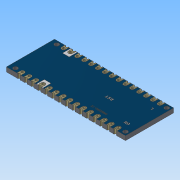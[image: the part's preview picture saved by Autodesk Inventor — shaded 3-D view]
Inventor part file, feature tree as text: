
AUTODESK INVENTOR PART (.ipt)
format: ipt  version: 2016 (Build 200138000, 138)  size: 3,481,600 bytes
history: native  units: mm
features: extrude x6, projected_geometry x6, sketch x5, other x3, hole x2, mirror x2, pattern_linear x1
ambient origin geometry x8: Origin, YZ Plane, XZ Plane, XY Plane, X Axis, Y Axis, Z Axis, Center Point
bodies: Body1 (feature_tree)
feature tree (25):
  other  "Blocks"
  extrude  "Extrusion4"  Depth=17.78mm
  sketch  "Sketch11"  dims[d9=1.6mm d10=0.0mm d11=1.27mm]
  hole  "Hole1"  [1 undecoded]
  hole  "Hole2"  [1 undecoded]
  extrude  "Extrusion5"  Depth=3.81mm
  pattern_linear  "Rectangular Pattern1"  Count1=15 Spacing1=35.56mm
  mirror  "Mirror1"
  mirror  "Mirror2"
  extrude  "Extrusion7"  Depth=1.6mm
  sketch  "Sketch15"  dims[d16=1.6mm d17=6.0mm d18=4.0mm d19=2.0mm d20=90.0deg d21=8.0mm d22=20.594885mm d23=0.9mm d24=6.0mm d25=4.0mm d26=2.0mm d27=90.0deg d28=8.0mm d29=20.594885mm d30=150.0mm d32=35.56mm d33=1.1mm d34=1.5mm d36=0.05mm d37=0.0mm d39=35.56mm d40=2.54mm d41=44.0mm d107=2.5mm d108=3.0mm d110=16.0mm d111=5.7mm d112=0.65mm d113=3.0mm d114=1.0mm d115=1.7mm d116=3.8mm d117=2.9mm d122=2.5mm d123=13.8mm d124=8.2mm d127=0.01mm d128=0.0mm d129=1.75mm d130=1.67mm d131=1.19mm d132=1.11mm d136=3.5mm d137=0.56mm d138=7.0mm d139=7.0mm d140=1.1mm d141=0.45mm d145=9.2mm d146=5.08mm d147=2.54mm d148=2.2mm d151=1.78mm d152=3.43mm d153=0.8mm d154=0.9mm d155=1.0625mm d156=2.7375mm d158=8.005mm d159=1.1mm d160=1.0625mm d161=2.7375mm d163=9.2mm d164=4.9mm d165=1.5mm d166=0.2mm d168=0.2mm d169=5.7mm d170=0.65mm d171=6.7mm d172=12.0mm d173=1.1mm d174=0.48125mm d175=0.103125mm d176=0.103125mm d177=0.103125mm d179=1.1mm d180=0.33mm d181=0.106562mm d182=0.103125mm d183=13.439035mm d184=9.250245mm d185=10.12291mm d186=0.488125mm d187=0.910937mm d193=1.1mm d195=0.055mm d196=0.055mm d197=0.11mm d198=0.935mm d199=0.165mm d200=0.165mm d202=2.55mm d203=0.3mm d204=11.0mm d205=1.0mm d206=0.5mm d209=2.2mm d212=2.2mm d213=90.0deg d214=1.0mm d215=0.9mm d216=0.1mm d218=3.3mm d219=0.1mm d221=8.0125mm d222=3.475mm d228=0.2mm d229=2.6mm d230=3.7mm d231=0.3mm d232=0.3mm d233=0.3mm d234=0.01mm d235=0.0mm d236=0.01mm d237=0.0mm d238=0.1mm d239=0.0mm d240=0.1mm d241=100.0mm d243=0.355556mm d244=10.0mm d246=10.0mm d250=80.0mm d252=0.3mm d253=10.0mm d255=10.0mm d257=0.05mm d258=0.05mm d259=3.7mm d261=0.2mm d262=0.2mm d264=1.6mm]
  extrude  "Extrusion8"  Depth=1.6mm
  extrude  "Extrusion9"  Depth=1.6mm TaperAngle=0.0deg
  extrude  "Extrusion10"  Depth=1.6mm
  sketch  "Sketch10"  dims[d7=44.0mm d8=17.78mm]
  projected_geometry  "Projected Loop1"
  sketch  "Sketch12"  dims[d12=1.27mm d13=2.09mm]
  projected_geometry  "Projected Loop2"
  sketch  "Sketch14"  dims[d14=1.27mm d15=3.81mm]
  projected_geometry  "Projected Loop4"
  projected_geometry  "Projected Loop5"
  projected_geometry  "Projected Loop6"
  projected_geometry  "Projected Loop7"
  other  "FCC Logo"
  other  "FCC Logo:1"
note: 2 required parameter values undecoded (feature->parameter linkage not recoverable at this tier; creation-order binding heuristic only, values carry confidence <= 0.55)
